# Revit family: Toilet-Floor_Mount-KOHLER-SAN_RAPHAEL-K-3722T_1
name_source: partatom
category: Plumbing Fixtures
revit_build: Autodesk Revit 2017 (Build: 20160225_1515(x64)
units: mm (PartAtom-declared; Revit-internal decimal feet)

## family parameters
Cut with Voids When Loaded = No
Host = Face
OmniClass Number = 23.31.19.00
OmniClass Title = Toilets
Part Type = Normal
Room Calculation Point = No
Round Connector Dimension = Use Diameter
Shared = No

## types (3) — shared parameters
ADA Compliant = No
Assembly Code = D2010100
CW Connection = Yes
Cold Water Inlet = Cold Water Inlet
Date Modified = 12/15/2020
Default Elevation = 0"
Description = Class 5 Skirted Trapway one-piece
Finish = Kohler-Vitreous_China-0-White
Flow Rate = 0 GPM
Flush Rate- GPF = 1.28 GPF
Flush Rate- LPF = 4.8 LPF
HW Connection = No
Height = 24"
Hot Water Inlet = Hot Water Inlet
Length = 29"
Manufacturer = KOHLER Co.
MasterFormat 2014 = 22 42 13.13
MasterFormat 2014 Name = Residential Water Closets
Material = Vitreous China
Pressure = 0.00 psi
Product Documentation Link = https://files.kohler.com.cn
Product Name = SAN RAPHAEL
Product Page URL = http://www.kohler.com.cn
Rough-In = 12"
Seat Included = Yes
URL = http://www.kohler.com.cn
Vent Connection = No
Waste Connection = Yes
Waste Water Outlet = Waste Water Outlet
Width = 20 1/2"

## per-type parameters (varying)
| type | Handle Material | Model | Type |
| Polished Chrome Handle, 0-White | Kohler-Metal-CP-Polished_Chrome | K-3722T-0 | 1 |
| Flange gold handle,0-White | Kohler-Metal-AF-Flange_Gold | K-3722T-SAF-0 | 2 |
| Rose Gold Handle,0-White | Kohler-Metal-RGD-Rose_Gold | K-3722T-SRGD-0 | 3 |

## geometry (parser evidence)
native form markers: Sweep x5
no freeform markers — native parametric forms only
